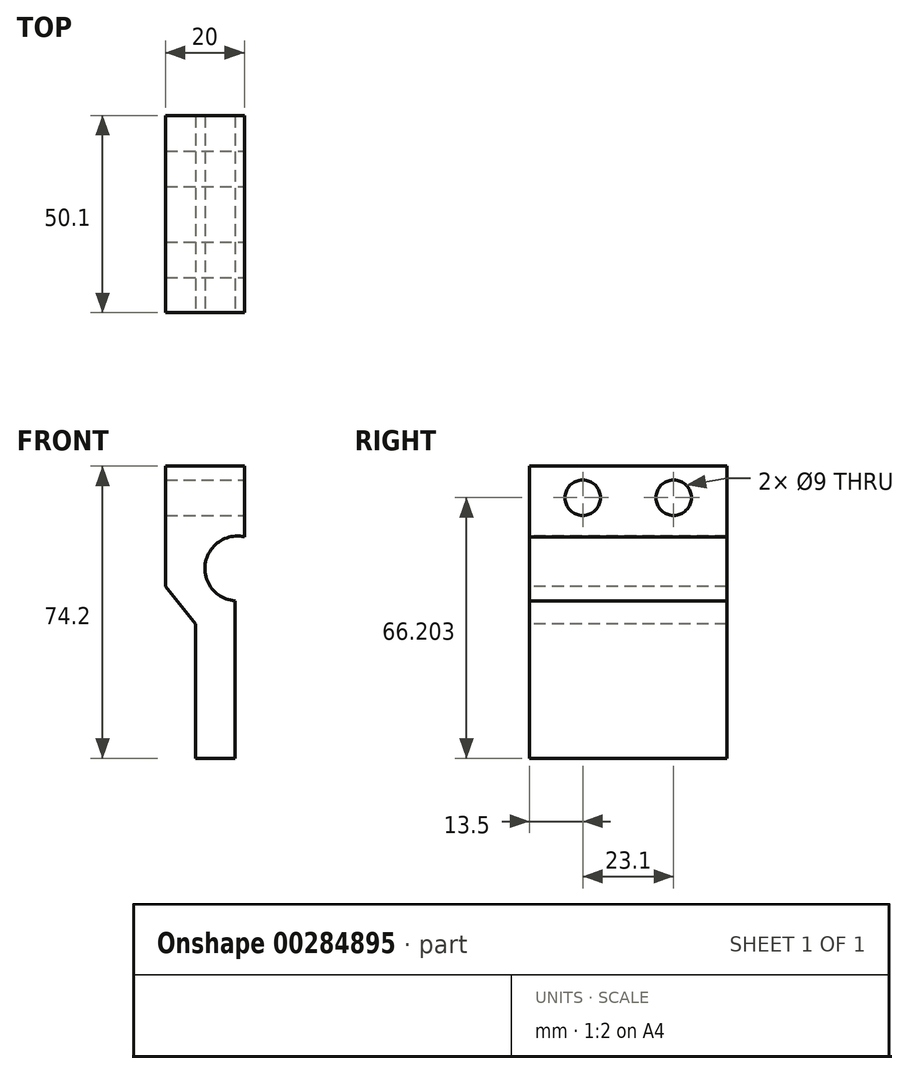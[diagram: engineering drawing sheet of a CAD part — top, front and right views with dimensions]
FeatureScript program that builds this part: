
annotation { "Feature Type Name" : "Feature", "Feature Type Description" : "" }
export const myFeature = defineFeature(function(context is Context, id is Id, definition is map)
    precondition{}
    {
        {
            var Q0;
            Q0=qCreatedBy(makeId("Front.planeOp"),FACE);
            var sketch = newSketch(context, id + "F0", { "sketchPlane" : qUnion([Q0])});
            skLineSegment(sketch, "E0", {"start": v(0, 38.12) * mm, "end": v(-20, 38.12) * mm});
            skLineSegment(sketch, "E1", {"start": v(0, 38.12) * mm, "end": v(0, 19.82) * mm});
            skLineSegment(sketch, "E2", {"start": v(-20, 38.12) * mm, "end": v(-20, 7.62) * mm});
            skLineSegment(sketch, "E3", {"start": v(-20, 7.62) * mm, "end": v(-12.4, -1.98) * mm});
            skLineSegment(sketch, "E4", {"start": v(-12.4, -1.98) * mm, "end": v(-12.4, -36.08) * mm});
            skLineSegment(sketch, "E5", {"start": v(-12.4, -36.08) * mm, "end": v(-2.4, -36.08) * mm});
            skLineSegment(sketch, "E6", {"start": v(-2.4, -36.08) * mm, "end": v(-2.4, 3.92) * mm});
            skArc(sketch, "E7", {"start": v(1.21, 19.82) * mm, "mid": v(-9.8, 13.96) * mm, "end": v(-2.4, 3.92) * mm});
            skSolve(sketch);
        }
        {
            var Q0;
            {var subQ1=sQuery(id+"F0.wireOp",EDGE,"E0");Q0=makeQuery(id+"F0.imprint","IMPRINT",FACE,{"disambiguationData":[TD([[makeQuery(id+"F0.imprint","IMPRINT",EDGE,{"derivedFrom":subQ1}),1.0]])]});}
            extrude(context, id + "F1", {"entities" : qUnion([Q0]), "oppositeDirection" : true, "depth" : 50.1 * mm, "offsetDistance" : 25.4 * mm});
        }
        {
            var Q0;
            Q0=makeQuery(id+"F1.opExtrude","SWEPT_FACE",FACE,{"disambiguationData":[OSD([sQuery(id+"F0.wireOp",EDGE,"E1")])]});
            var sketch = newSketch(context, id + "F2", { "sketchPlane" : qUnion([Q0])});
            skPoint(sketch, "E8", {"position": v(13.5, 30.12) * mm});
            skPoint(sketch, "E9", {"position": v(36.6, 30.12) * mm});
            skSolve(sketch);
        }
        {
            var Q0;
            Q0=sQuery(id+"F2.wireOp",VERTEX,"E8");
            var Q1;
            Q1=sQuery(id+"F2.wireOp",VERTEX,"E9");
            var Q2;
            Q2=makeQuery(id+"F1.opExtrude","SWEPT_BODY",BODY,{"disambiguationData":[OSD([sQuery(id+"F0.wireOp",EDGE,"E0"),sQuery(id+"F0.wireOp",EDGE,"E1"),sQuery(id+"F0.wireOp",EDGE,"E2"),sQuery(id+"F0.wireOp",EDGE,"E3"),sQuery(id+"F0.wireOp",EDGE,"E4"),sQuery(id+"F0.wireOp",EDGE,"E5"),sQuery(id+"F0.wireOp",EDGE,"E6"),sQuery(id+"F0.wireOp",EDGE,"E7")])]});
            hole(context, id + "F3", {"style" : HoleStyle.SIMPLE, "endStyle" : HoleEndStyle.THROUGH, "standardTappedOrClearance" : lookupTablePath({ "fit" : "Normal", "standard" : "ISO", "size" : "M8", "type" : "Clearance" }), "standardBlindInLast" : lookupTablePath({ "fit" : "Normal", "standard" : "ISO", "engagement" : "75%", "pitch" : "1.25 mm", "size" : "M8", "type" : "Clearance & tapped" }), "holeDiameter" : 9 * mm, "majorDiameter" : 6.35 * mm, "isTappedThrough" : true, "tappedDepth" : 12.7 * mm, "tapClearance" : 3, "locations" : qUnion([Q0, Q1]), "scope" : qUnion([Q2])});
        }
    });
